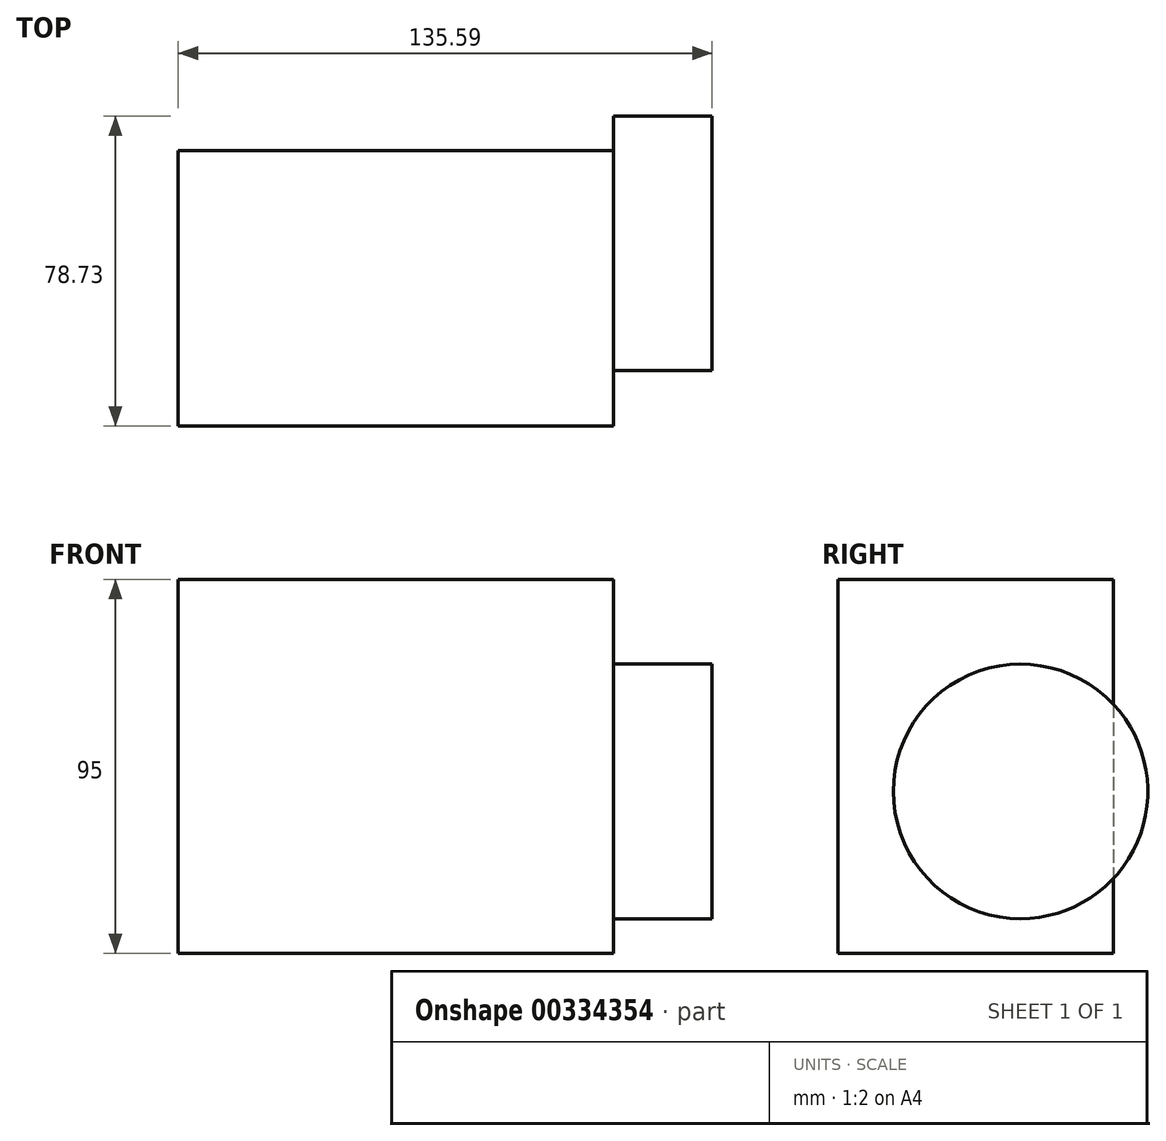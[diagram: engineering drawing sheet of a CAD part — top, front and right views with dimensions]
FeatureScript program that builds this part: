
annotation { "Feature Type Name" : "Feature", "Feature Type Description" : "" }
export const myFeature = defineFeature(function(context is Context, id is Id, definition is map)
    precondition{}
    {
        {
            var Q0;
            Q0=qCreatedBy(makeId("Top.planeOp"),FACE);
            var sketch = newSketch(context, id + "F0", { "sketchPlane" : qUnion([Q0])});
            skLineSegment(sketch, "E0.bottom", {"start": v(0, 0) * mm, "end": v(50, 0) * mm});
            skLineSegment(sketch, "E0.top", {"start": v(0, 70) * mm, "end": v(50, 70) * mm});
            skLineSegment(sketch, "E0.left", {"start": v(0, 0) * mm, "end": v(0, 70) * mm});
            skLineSegment(sketch, "E0.right", {"start": v(50, 0) * mm, "end": v(50, 70) * mm});
            skSolve(sketch);
        }
        {
            var Q0;
            Q0=makeQuery(id+"F0.imprint","IMPRINT",FACE,{"disambiguationData":[TD([[makeQuery(id+"F0.imprint","IMPRINT",EDGE,{"derivedFrom":sQuery(id+"F0.wireOp",EDGE,"E0.bottom")}),1.0]])]});
            extrude(context, id + "F1", {"entities" : qUnion([Q0]), "depth" : 95 * mm});
        }
        {
            var Q0;
            Q0=makeQuery(id+"F1.opExtrude","SWEPT_FACE",FACE,{"disambiguationData":[OSD([sQuery(id+"F0.wireOp",EDGE,"E0.right")])]});
            extrude(context, id + "F2", {"entities" : qUnion([Q0]), "operationType" : NewBodyOperationType.ADD, "depth" : 60.6 * mm});
        }
        {
            var Q0;
            Q0=makeQuery(id+"F2.opExtrude","CAP_FACE",FACE,{"disambiguationData":[OSD([sQuery(id+"F0.wireOp",EDGE,"E0.right")])],"isStart":false});
            var sketch = newSketch(context, id + "F3", { "sketchPlane" : qUnion([Q0])});
            skCircle(sketch, "E1", {"center": v(46.4, 41.15) * mm, "radius": 32.33 * mm});
            skSolve(sketch);
        }
        {
            var Q0;
            Q0 = qSketchRegion(id + "F3", true);
            extrude(context, id + "F4", {"entities" : qUnion([Q0]), "operationType" : NewBodyOperationType.ADD, "depth" : 25 * mm});
        }
        {
            var Q0;
            Q0=makeQuery(id+"F4.opExtrude","CAP_FACE",FACE,{"disambiguationData":[OSD([sQuery(id+"F3.wireOp",EDGE,"E1")])],"isStart":false});
            var sketch = newSketch(context, id + "F5", { "sketchPlane" : qUnion([Q0])});
            skCircle(sketch, "E2", {"center": v(46.4, 41.15) * mm, "radius": 16.33 * mm});
            skSolve(sketch);
        }
        {
            var Q0;
            Q0=makeQuery(id+"F5.imprint","IMPRINT",FACE,{"disambiguationData":[TD([[makeQuery(id+"F5.imprint","IMPRINT",EDGE,{"derivedFrom":sQuery(id+"F5.wireOp",EDGE,"E2")}),1.0]])]});
            var Q1;
            Q1 = qSketchRegion(id + "F5", true);
            extrude(context, id + "F6", {"entities" : qUnion([Q0, Q1]), "operationType" : NewBodyOperationType.ADD, "depth" : -10 * mm});
        }
    });
